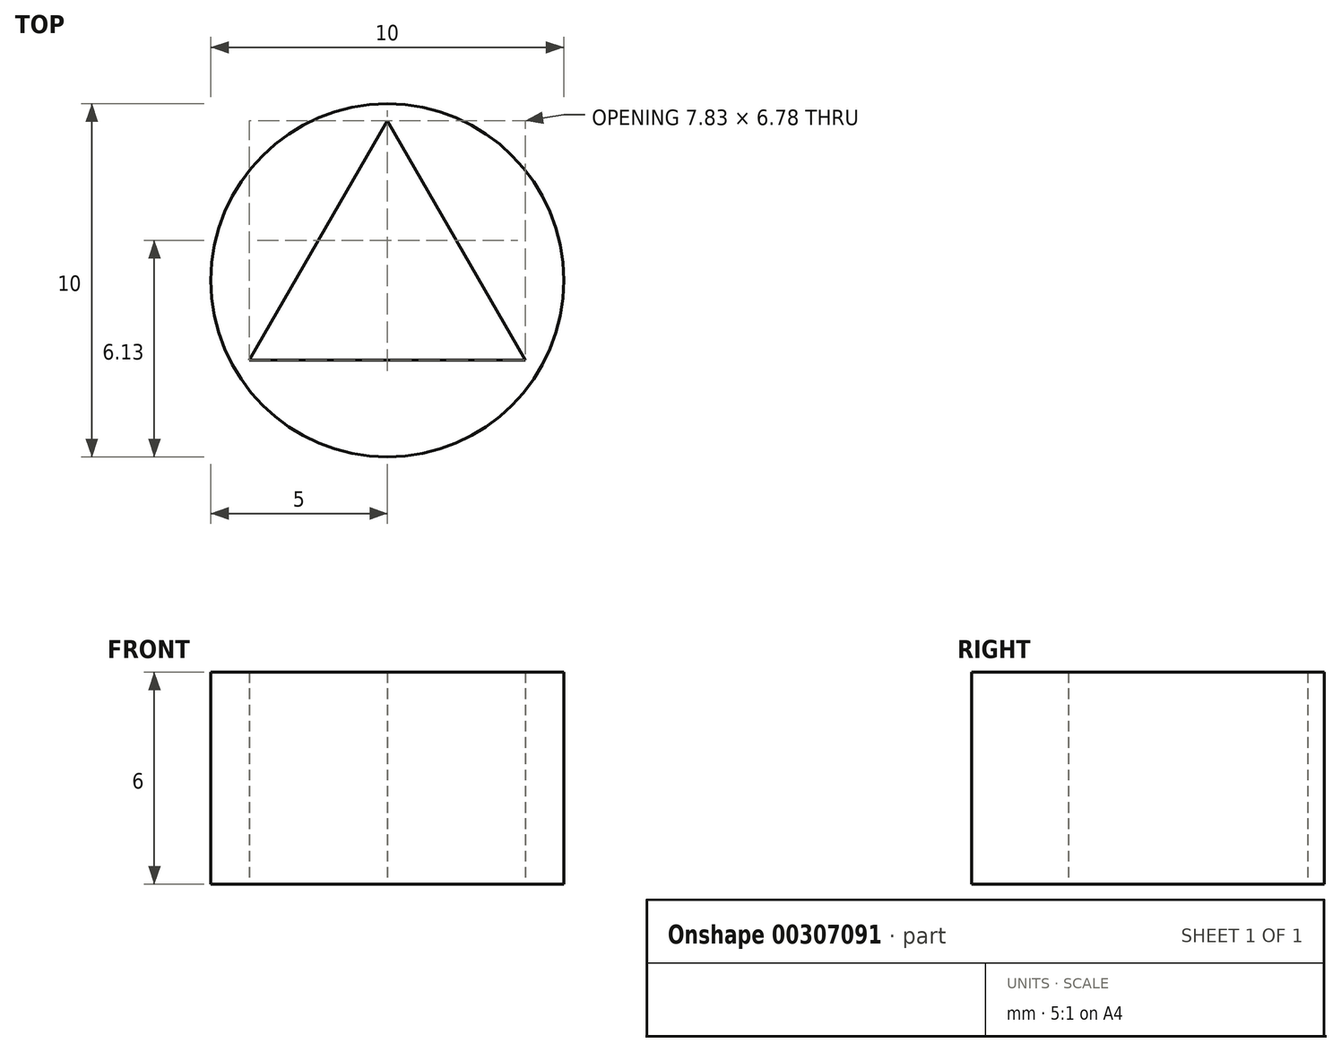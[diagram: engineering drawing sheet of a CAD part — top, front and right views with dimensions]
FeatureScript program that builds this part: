
annotation { "Feature Type Name" : "Feature", "Feature Type Description" : "" }
export const myFeature = defineFeature(function(context is Context, id is Id, definition is map)
    precondition{}
    {
        {
            assignVariable(context, id + "F0", {"name" : "Height", "anyValue" : 6});
        }
        {
            var Q0;
            Q0=qCreatedBy(makeId("Top.planeOp"),FACE);
            var sketch = newSketch(context, id + "F1", { "sketchPlane" : qUnion([Q0])});
            skCircle(sketch, "E0", {"center": v(0, 0) * mm, "radius": 5 * mm});
            skCircle(sketch, "E1.cCircle", {"center": v(0, 0) * mm, "radius": 2.26 * mm, "construction": true});
            skLineSegment(sketch, "E1.0", {"start": v(0, 4.52) * mm, "end": v(3.91, -2.26) * mm});
            skLineSegment(sketch, "E1.1", {"start": v(3.92, -2.26) * mm, "end": v(-3.92, -2.26) * mm});
            skLineSegment(sketch, "E1.2", {"start": v(-3.92, -2.26) * mm, "end": v(0, 4.52) * mm});
            skPoint(sketch, "E1.0.midPoint", {"position": v(1.96, 1.13) * mm});
            skSolve(sketch);
        }
        {
            var Q0;
            Q0=makeQuery(id+"F1.imprint","IMPRINT",FACE,{"disambiguationData":[TD([[makeQuery(id+"F1.imprint","IMPRINT",EDGE,{"derivedFrom":sQuery(id+"F1.wireOp",EDGE,"E0")}),1.0]])]});
            extrude(context, id + "F2", {"entities" : qUnion([Q0]), "depth" : (getVariable(context, 'Height')) * mm});
        }
    });
